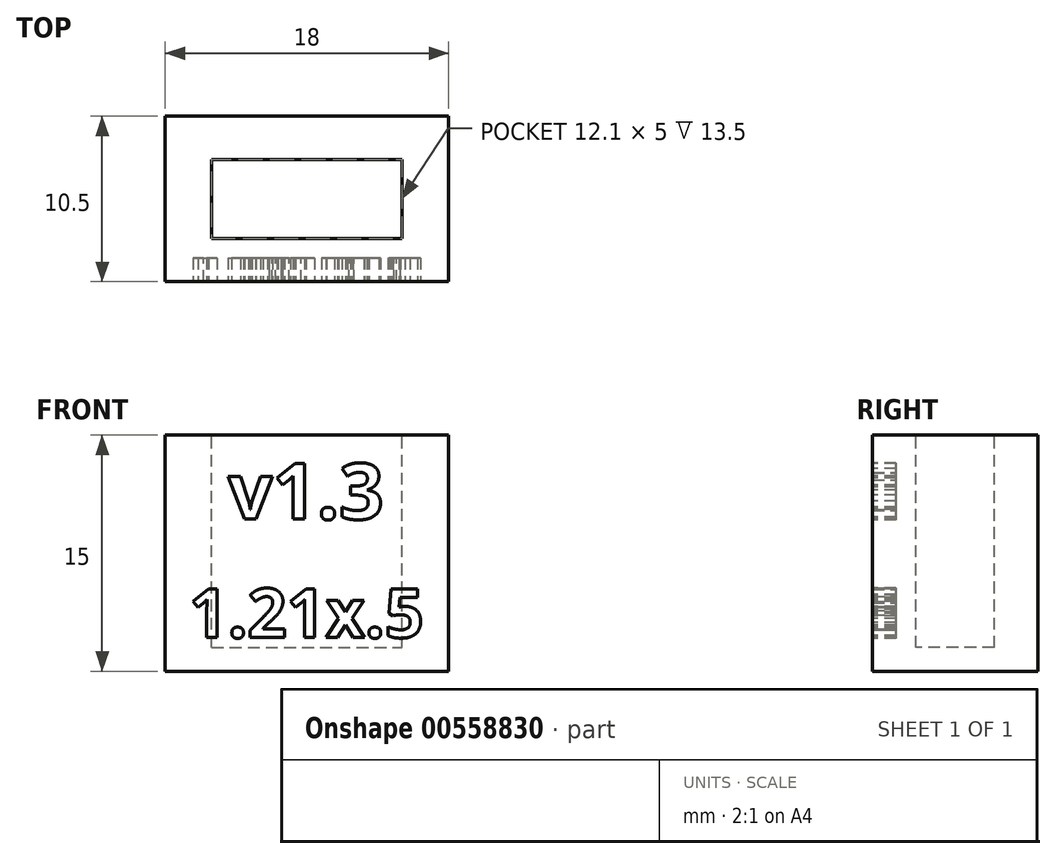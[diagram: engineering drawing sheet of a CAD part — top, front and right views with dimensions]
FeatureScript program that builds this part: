
annotation { "Feature Type Name" : "Feature", "Feature Type Description" : "" }
export const myFeature = defineFeature(function(context is Context, id is Id, definition is map)
    precondition{}
    {
        {
            var Q0;
            Q0=qCreatedBy(makeId("Top.planeOp"),FACE);
            var sketch = newSketch(context, id + "F0", { "sketchPlane" : qUnion([Q0])});
            skLineSegment(sketch, "E0.0", {"start": v(9, 5.25) * mm, "end": v(-9, 5.25) * mm});
            skLineSegment(sketch, "E0.1", {"start": v(9, 5.25) * mm, "end": v(9, -5.25) * mm});
            skLineSegment(sketch, "E0.2", {"start": v(9, -5.25) * mm, "end": v(-9, -5.25) * mm});
            skLineSegment(sketch, "E0.3", {"start": v(-9, 5.25) * mm, "end": v(-9, -5.25) * mm});
            skSolve(sketch);
        }
        {
            var Q0;
            Q0=makeQuery(id+"F0.imprint","IMPRINT",FACE,{"disambiguationData":[TD([[makeQuery(id+"F0.imprint","IMPRINT",EDGE,{"derivedFrom":sQuery(id+"F0.wireOp",EDGE,"E0.0")}),1.0]])]});
            extrude(context, id + "F1", {"entities" : qUnion([Q0]), "endBound" : BoundingType.SYMMETRIC, "depth" : 15 * mm, "offsetDistance" : 25 * mm});
        }
        {
            var Q0;
            Q0=makeQuery(id+"F1.opExtrude","CAP_FACE",FACE,{"disambiguationData":[OSD([sQuery(id+"F0.wireOp",EDGE,"E0.0"),sQuery(id+"F0.wireOp",EDGE,"E0.1"),sQuery(id+"F0.wireOp",EDGE,"E0.2"),sQuery(id+"F0.wireOp",EDGE,"E0.3")])],"isStart":false});
            var sketch = newSketch(context, id + "F2", { "sketchPlane" : qUnion([Q0])});
            skLineSegment(sketch, "E1.bottom", {"start": v(-6.05, 2.5) * mm, "end": v(6.05, 2.5) * mm});
            skLineSegment(sketch, "E1.top", {"start": v(-6.05, -2.5) * mm, "end": v(6.05, -2.5) * mm});
            skLineSegment(sketch, "E1.left", {"start": v(-6.05, 2.5) * mm, "end": v(-6.05, -2.5) * mm});
            skLineSegment(sketch, "E1.right", {"start": v(6.05, 2.5) * mm, "end": v(6.05, -2.5) * mm});
            skPoint(sketch, "E1.middle", {"position": v(0, 0) * mm});
            skSolve(sketch);
        }
        {
            var Q0;
            Q0=makeQuery(id+"F2.imprint","IMPRINT",FACE,{"disambiguationData":[TD([[makeQuery(id+"F2.imprint","IMPRINT",EDGE,{"derivedFrom":sQuery(id+"F2.wireOp",EDGE,"E1.bottom")}),-1.0]])]});
            extrude(context, id + "F3", {"entities" : qUnion([Q0]), "operationType" : NewBodyOperationType.REMOVE, "oppositeDirection" : true, "depth" : 13.5 * mm, "offsetDistance" : 25 * mm});
        }
        {
            var Q0;
            Q0=makeQuery(id+"F1.opExtrude","SWEPT_FACE",FACE,{"disambiguationData":[OSD([sQuery(id+"F0.wireOp",EDGE,"E0.2")])]});
            var sketch = newSketch(context, id + "F4", { "sketchPlane" : qUnion([Q0])});
            skText(sketch, "E2", { "text": "v1.3", "fontName": "OpenSans-Bold.ttf"});
            skText(sketch, "E3", { "text": "1.21x.5", "fontName": "OpenSans-Bold.ttf"});
            const initialGuessF4  = {"E2": [-0.005, 0.00216, 1, 0, 0.00356], "E3": [-0.0075, -0.00536, 1, 0, 0.00313]};
            skSetInitialGuess(sketch, initialGuessF4);
            skSolve(sketch);
        }
        {
            var Q0;
            Q0 = qSketchRegion(id + "F4", true);
            extrude(context, id + "F5", {"entities" : qUnion([Q0]), "operationType" : NewBodyOperationType.REMOVE, "oppositeDirection" : true, "depth" : 1.5 * mm, "offsetDistance" : 25 * mm});
        }
    });
